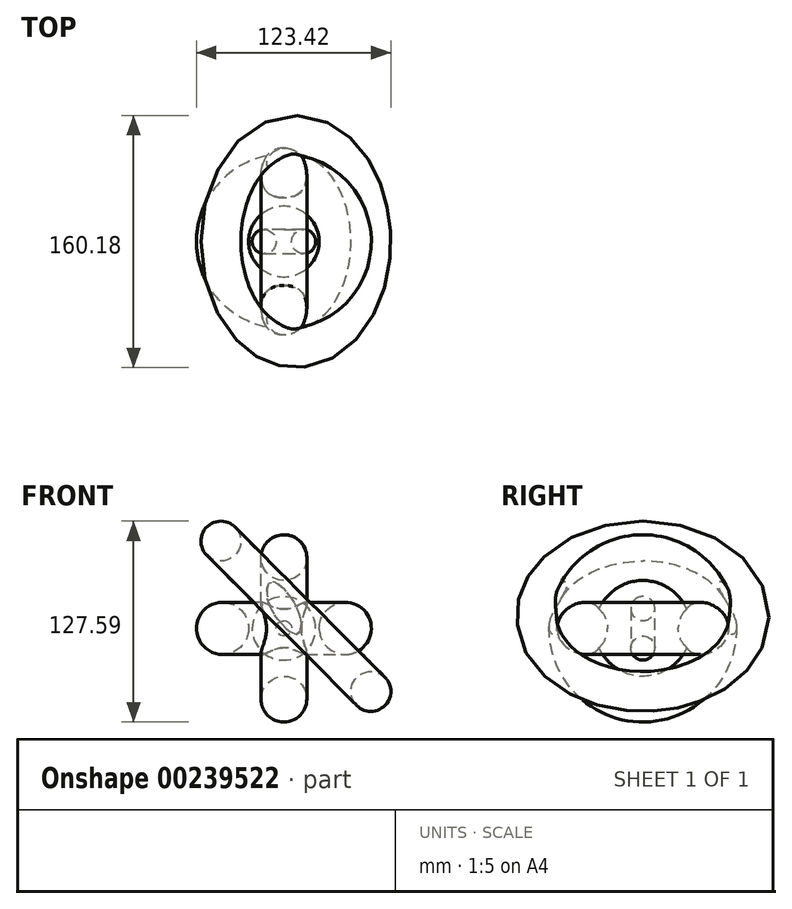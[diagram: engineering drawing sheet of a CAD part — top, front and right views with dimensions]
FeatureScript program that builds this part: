
annotation { "Feature Type Name" : "Feature", "Feature Type Description" : "" }
export const myFeature = defineFeature(function(context is Context, id is Id, definition is map)
    precondition{}
    {
        {
            var Q0;
            Q0=qCreatedBy(makeId("Front.planeOp"),FACE);
            var sketch = newSketch(context, id + "F0", { "sketchPlane" : qUnion([Q0])});
            skCircle(sketch, "E0", {"center": v(38.98, 0) * mm, "radius": 16.55 * mm});
            skLineSegment(sketch, "E1", {"start": v(0, 33.6) * mm, "end": v(0, -33.4) * mm});
            skSolve(sketch);
        }
        {
            var Q0;
            Q0 = qSketchRegion(id + "F0", true);
            var Q1;
            Q1=sQuery(id+"F0.wireOp",EDGE,"E1");
            revolve(context, id + "F1", {"entities" : qUnion([Q0]), "axis" : qUnion([Q1]), "revolveType" : RevolveType.FULL});
        }
        {
            var Q0;
            Q0=qCreatedBy(makeId("Top.planeOp"),FACE);
            var sketch = newSketch(context, id + "F2", { "sketchPlane" : qUnion([Q0])});
            skCircle(sketch, "E2", {"center": v(-12.54, 0) * mm, "radius": 7.64 * mm});
            skLineSegment(sketch, "E3", {"start": v(0, 14.79) * mm, "end": v(0, -14) * mm});
            skSolve(sketch);
        }
        {
            var Q0;
            Q0 = qSketchRegion(id + "F2", true);
            var Q1;
            Q1=sQuery(id+"F2.wireOp",EDGE,"E3");
            revolve(context, id + "F3", {"entities" : qUnion([Q0]), "axis" : qUnion([Q1]), "revolveType" : RevolveType.FULL});
        }
        {
            var Q0;
            Q0=qCreatedBy(makeId("Front.planeOp"),FACE);
            var sketch = newSketch(context, id + "F4", { "sketchPlane" : qUnion([Q0])});
            skCircle(sketch, "E4", {"center": v(0, 44.95) * mm, "radius": 14.54 * mm});
            skLineSegment(sketch, "E5", {"start": v(59.15, 0) * mm, "end": v(-64.24, 0) * mm});
            skSolve(sketch);
        }
        {
            var Q0;
            Q0 = qSketchRegion(id + "F4", true);
            var Q1;
            Q1=sQuery(id+"F4.wireOp",EDGE,"E5");
            revolve(context, id + "F5", {"operationType" : NewBodyOperationType.ADD, "entities" : qUnion([Q0]), "axis" : qUnion([Q1]), "revolveType" : RevolveType.FULL});
        }
        {
            var Q0;
            Q0=qCreatedBy(makeId("Front.planeOp"),FACE);
            var sketch = newSketch(context, id + "F6", { "sketchPlane" : qUnion([Q0])});
            skCircle(sketch, "E6", {"center": v(55.23, -40.05) * mm, "radius": 12.66 * mm});
            skLineSegment(sketch, "E7", {"start": v(76.39, 76.29) * mm, "end": v(-76, -75.7) * mm});
            skSolve(sketch);
        }
        {
            var Q0;
            Q0 = qSketchRegion(id + "F6", true);
            var Q1;
            Q1=sQuery(id+"F6.wireOp",EDGE,"E7");
            revolve(context, id + "F7", {"operationType" : NewBodyOperationType.ADD, "entities" : qUnion([Q0]), "axis" : qUnion([Q1]), "revolveType" : RevolveType.FULL});
        }
    });
